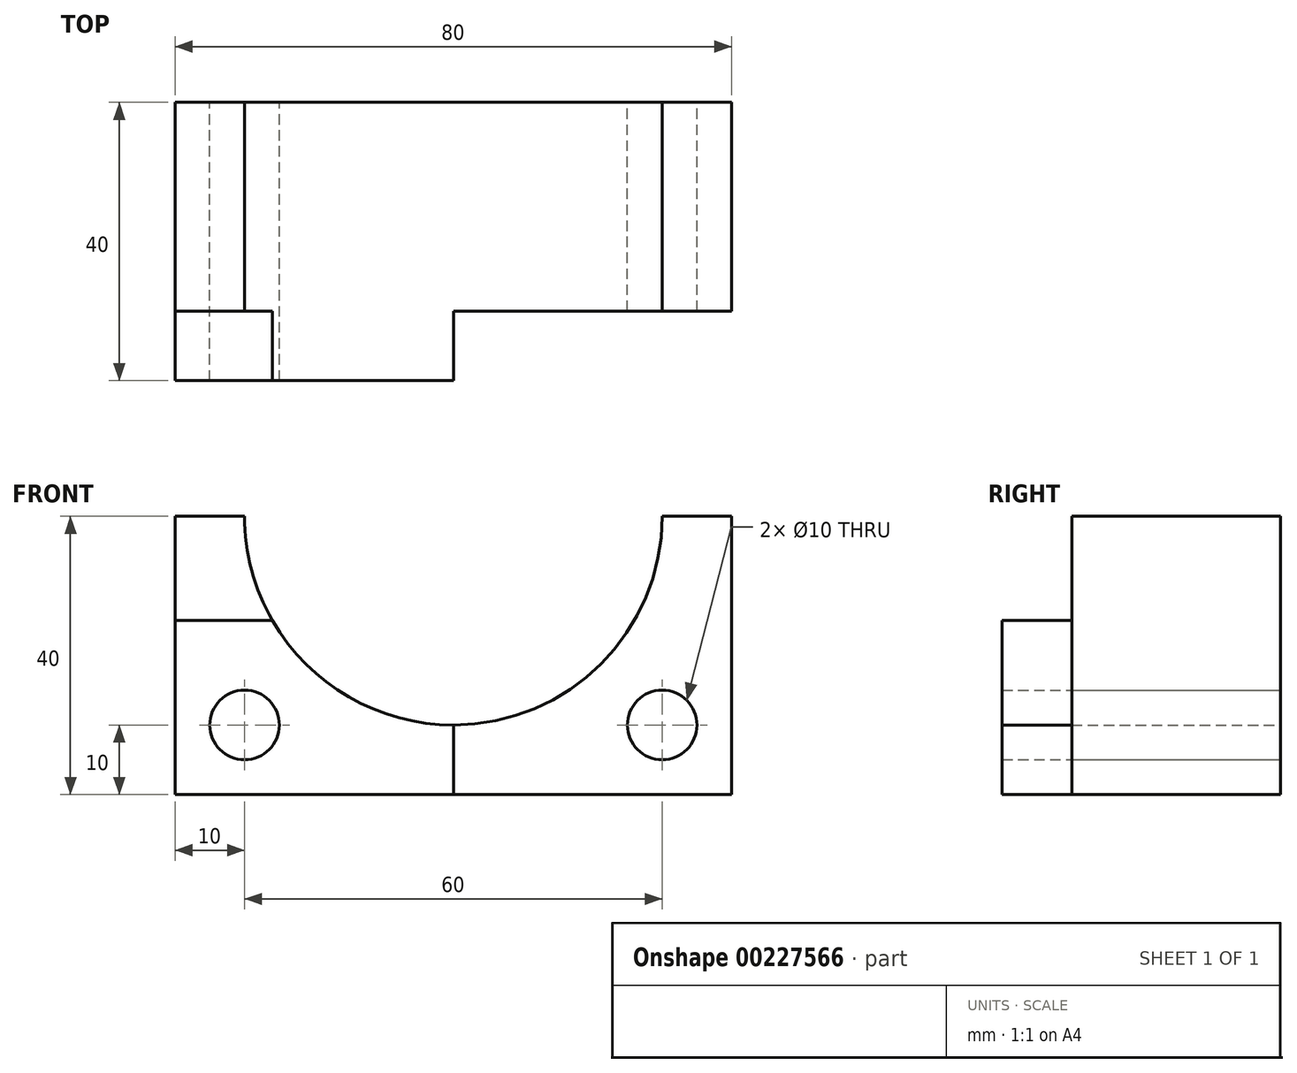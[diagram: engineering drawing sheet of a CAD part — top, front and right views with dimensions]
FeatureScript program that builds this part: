
annotation { "Feature Type Name" : "Feature", "Feature Type Description" : "" }
export const myFeature = defineFeature(function(context is Context, id is Id, definition is map)
    precondition{}
    {
        {
            var Q0;
            Q0=qCreatedBy(makeId("Front.planeOp"),FACE);
            var sketch = newSketch(context, id + "F0", { "sketchPlane" : qUnion([Q0])});
            skLineSegment(sketch, "E0.bottom", {"start": v(0, 40) * mm, "end": v(10, 40) * mm});
            skLineSegment(sketch, "E0.top", {"start": v(0, 0) * mm, "end": v(80, 0) * mm});
            skLineSegment(sketch, "E0.left", {"start": v(0, 40) * mm, "end": v(0, 0) * mm});
            skLineSegment(sketch, "E0.right", {"start": v(80, 40) * mm, "end": v(80, 0) * mm});
            skArc(sketch, "E1", {"start": v(10, 40) * mm, "mid": v(40, 10) * mm, "end": v(70, 40) * mm});
            skLineSegment(sketch, "E2.trimOffspring", {"start": v(70, 40) * mm, "end": v(80, 40) * mm});
            skLineSegment(sketch, "E3", {"start": v(0, 25) * mm, "end": v(14.02, 25) * mm});
            skPoint(sketch, "E4", {"position": v(40, 0) * mm});
            skLineSegment(sketch, "E5", {"start": v(40, 0) * mm, "end": v(40, 10) * mm});
            skCircle(sketch, "E6", {"center": v(10, 10) * mm, "radius": 5 * mm});
            skCircle(sketch, "E7", {"center": v(70, 10) * mm, "radius": 5 * mm});
            skSolve(sketch);
        }
        {
            var Q0;
            {var subQ0=sQuery(id+"F0.wireOp",EDGE,"E3");Q0=makeQuery(id+"F0.imprint","IMPRINT",FACE,{"disambiguationData":[TD([[makeQuery(id+"F0.imprint","IMPRINT",EDGE,{"derivedFrom":subQ0}),-1.0]])]});}
            extrude(context, id + "F1", {"entities" : qUnion([Q0]), "depth" : 40 * mm});
        }
        {
            var Q0;
            {var subQ1=sQuery(id+"F0.wireOp",EDGE,"E0.right");Q0=makeQuery(id+"F0.imprint","IMPRINT",FACE,{"disambiguationData":[TD([[makeQuery(id+"F0.imprint","IMPRINT",EDGE,{"derivedFrom":subQ1}),-1.0]])]});}
            var Q1;
            {var subQ0=sQuery(id+"F0.wireOp",EDGE,"E0.bottom");Q1=makeQuery(id+"F0.imprint","IMPRINT",FACE,{"disambiguationData":[TD([[makeQuery(id+"F0.imprint","IMPRINT",EDGE,{"derivedFrom":subQ0}),-1.0]])]});}
            extrude(context, id + "F2", {"entities" : qUnion([Q0, Q1]), "operationType" : NewBodyOperationType.ADD, "depth" : 30 * mm});
        }
    });
